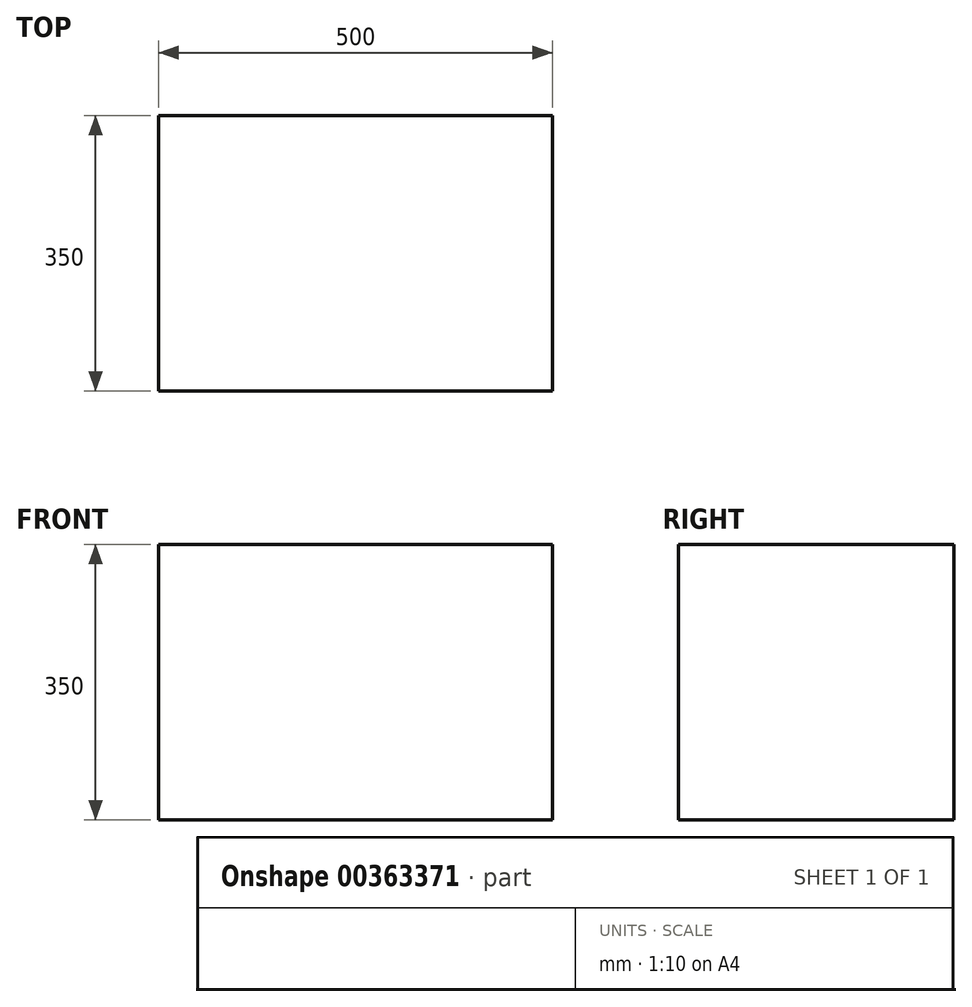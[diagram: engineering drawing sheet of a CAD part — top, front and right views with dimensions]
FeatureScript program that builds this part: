
annotation { "Feature Type Name" : "Feature", "Feature Type Description" : "" }
export const myFeature = defineFeature(function(context is Context, id is Id, definition is map)
    precondition{}
    {
        {
            var Q0;
            Q0=qCreatedBy(makeId("Top.planeOp"),FACE);
            var sketch = newSketch(context, id + "F0", { "sketchPlane" : qUnion([Q0])});
            skLineSegment(sketch, "E0.bottom", {"start": v(0, 0) * mm, "end": v(500, 0) * mm});
            skLineSegment(sketch, "E0.top", {"start": v(0, 350) * mm, "end": v(500, 350) * mm});
            skLineSegment(sketch, "E0.left", {"start": v(0, 0) * mm, "end": v(0, 350) * mm});
            skLineSegment(sketch, "E0.right", {"start": v(500, 0) * mm, "end": v(500, 350) * mm});
            skSolve(sketch);
        }
        {
            var Q0;
            Q0=makeQuery(id+"F0.imprint","IMPRINT",FACE,{"disambiguationData":[TD([[makeQuery(id+"F0.imprint","IMPRINT",EDGE,{"derivedFrom":sQuery(id+"F0.wireOp",EDGE,"E0.bottom")}),1.0]])]});
            extrude(context, id + "F1", {"entities" : qUnion([Q0]), "depth" : 350 * mm});
        }
    });
